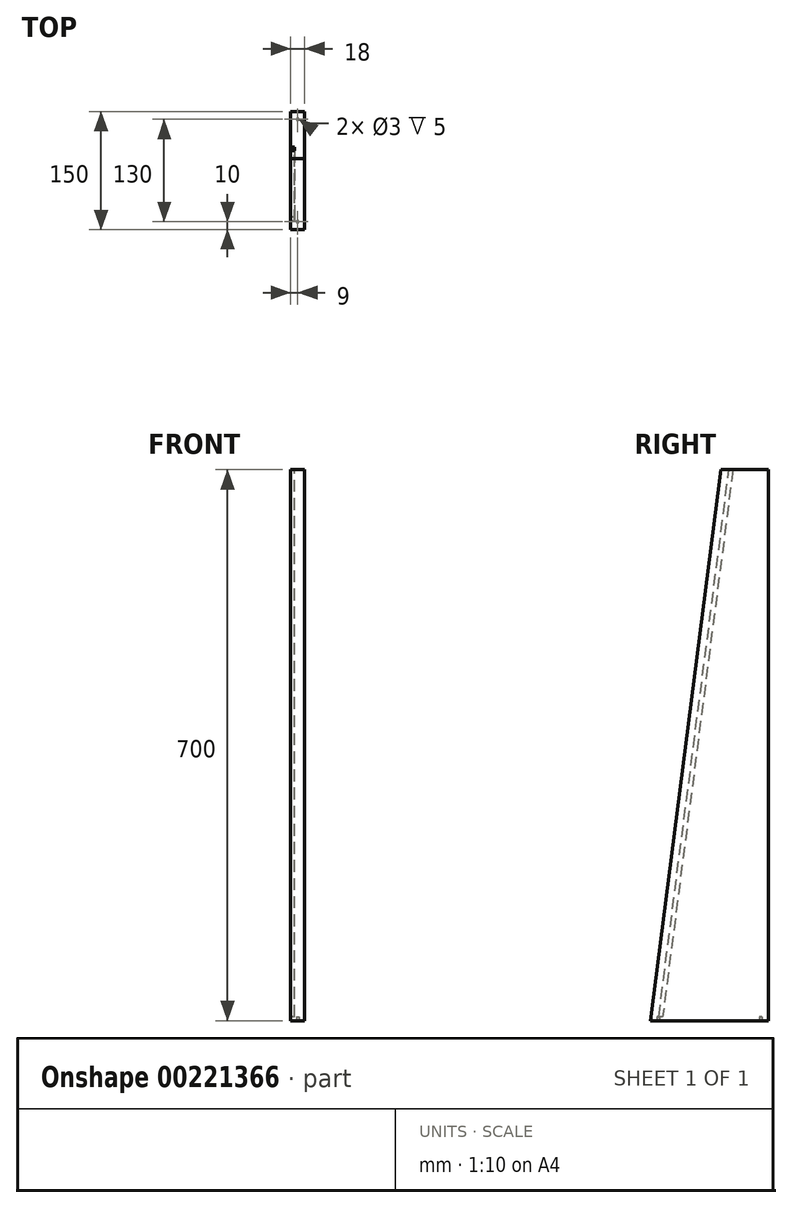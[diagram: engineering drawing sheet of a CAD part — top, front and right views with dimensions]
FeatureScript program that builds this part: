
annotation { "Feature Type Name" : "Feature", "Feature Type Description" : "" }
export const myFeature = defineFeature(function(context is Context, id is Id, definition is map)
    precondition{}
    {
        {
            var Q0;
            Q0=qCreatedBy(makeId("Right.planeOp"),FACE);
            var sketch = newSketch(context, id + "F0", { "sketchPlane" : qUnion([Q0])});
            skLineSegment(sketch, "E0", {"start": v(0, 0) * mm, "end": v(150, 0) * mm});
            skLineSegment(sketch, "E1", {"start": v(150, 0) * mm, "end": v(150, 700) * mm});
            skLineSegment(sketch, "E2", {"start": v(150, 700) * mm, "end": v(90, 700) * mm});
            skLineSegment(sketch, "E3", {"start": v(90, 700) * mm, "end": v(0, 0) * mm});
            skSolve(sketch);
        }
        {
            var Q0;
            Q0=qSketchRegion(id+"F0",true);
            extrude(context, id + "F1", {"entities" : qUnion([Q0]), "depth" : 18 * mm});
        }
        {
            var Q0;
            Q0=makeQuery(id+"F1.opExtrude","CAP_FACE",FACE,{"disambiguationData":[OSD([sQuery(id+"F0.wireOp",EDGE,"E0"),sQuery(id+"F0.wireOp",EDGE,"E1"),sQuery(id+"F0.wireOp",EDGE,"E2"),sQuery(id+"F0.wireOp",EDGE,"E3")])],"isStart":true});
            var sketch = newSketch(context, id + "F2", { "sketchPlane" : qUnion([Q0])});
            skLineSegment(sketch, "E4", {"start": v(-10.64, 5) * mm, "end": v(-100, 700) * mm});
            skLineSegment(sketch, "E5", {"start": v(-100, 700) * mm, "end": v(-105, 700) * mm});
            skLineSegment(sketch, "E6", {"start": v(-105, 700) * mm, "end": v(-15.64, 5) * mm});
            skLineSegment(sketch, "E7", {"start": v(-15.64, 5) * mm, "end": v(-10.64, 5) * mm});
            skPoint(sketch, "E8.start.orphan", {"position": v(-15, 0) * mm});
            skPoint(sketch, "E9.orphan", {"position": v(-10, 0) * mm});
            skSolve(sketch);
        }
        {
            var Q0;
            Q0 = qSketchRegion(id + "F2", true);
            extrude(context, id + "F3", {"entities" : qUnion([Q0]), "operationType" : NewBodyOperationType.REMOVE, "oppositeDirection" : true, "depth" : 5 * mm});
        }
        {
            var Q0;
            Q0=makeQuery(id+"F1.opExtrude","SWEPT_FACE",FACE,{"disambiguationData":[OSD([sQuery(id+"F0.wireOp",EDGE,"E0")])]});
            var sketch = newSketch(context, id + "F4", { "sketchPlane" : qUnion([Q0])});
            skCircle(sketch, "E10", {"center": v(9, -10) * mm, "radius": 1.5 * mm});
            skCircle(sketch, "E11", {"center": v(9, -140) * mm, "radius": 1.5 * mm});
            skSolve(sketch);
        }
        {
            var Q0;
            Q0 = qSketchRegion(id + "F4", true);
            extrude(context, id + "F5", {"entities" : qUnion([Q0]), "operationType" : NewBodyOperationType.REMOVE, "oppositeDirection" : true, "depth" : 5 * mm});
        }
    });
